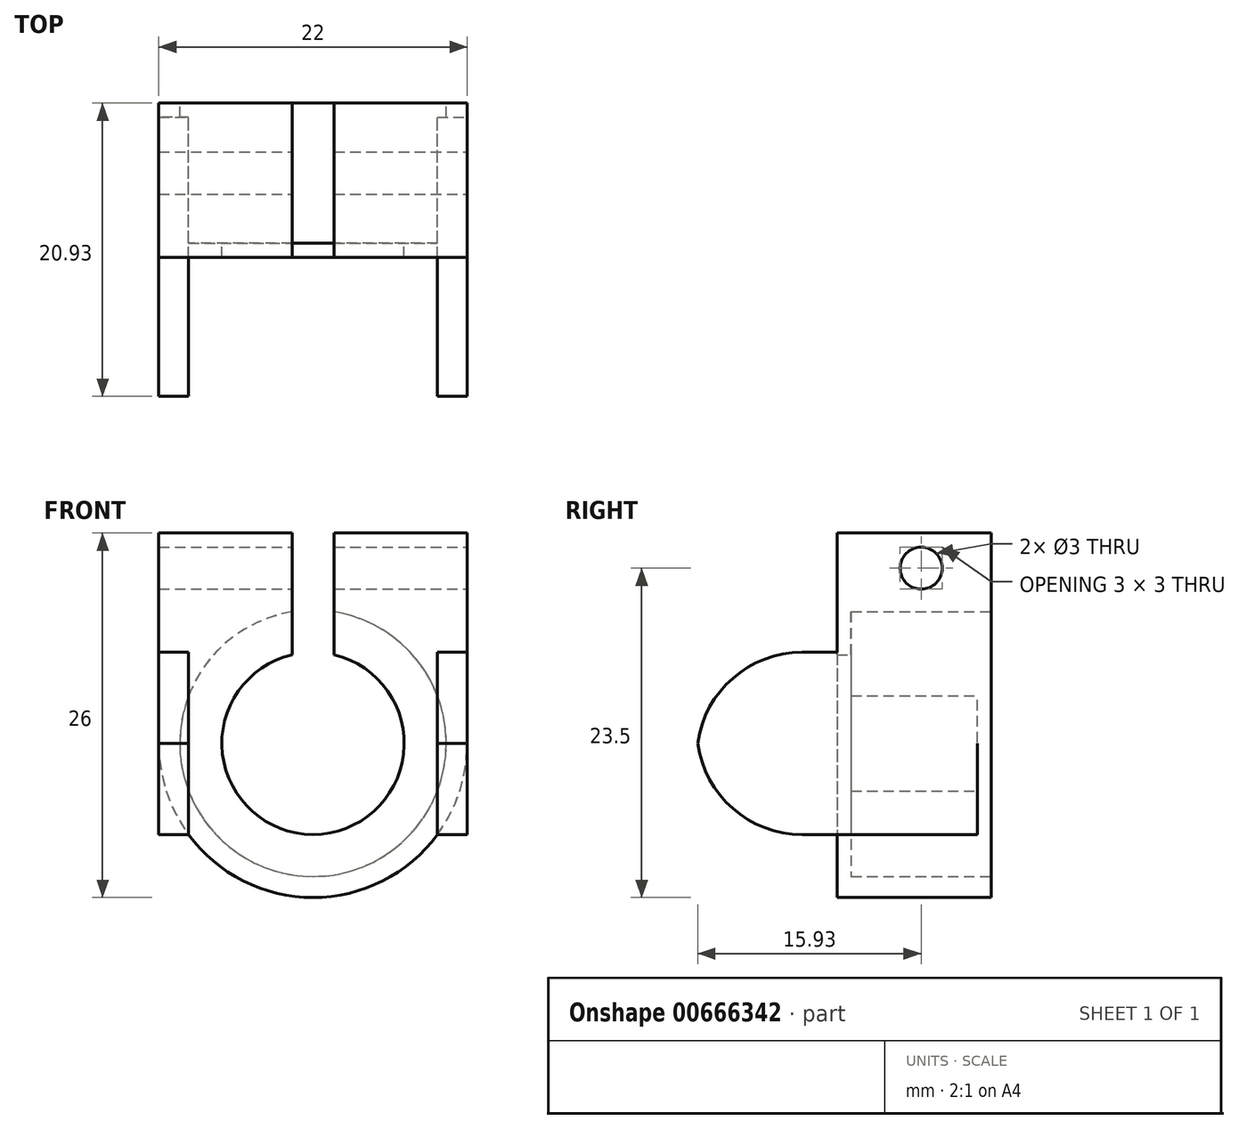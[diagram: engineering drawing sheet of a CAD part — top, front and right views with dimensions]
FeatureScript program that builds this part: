
annotation { "Feature Type Name" : "Feature", "Feature Type Description" : "" }
export const myFeature = defineFeature(function(context is Context, id is Id, definition is map)
    precondition{}
    {
        {
            var Q0;
            Q0=qCreatedBy(makeId("Front.planeOp"),FACE);
            var sketch = newSketch(context, id + "F0", { "sketchPlane" : qUnion([Q0])});
            skArc(sketch, "E0", {"start": v(-1.5, 9.38) * mm, "mid": v(0, -9.5) * mm, "end": v(1.5, 9.38) * mm});
            skArc(sketch, "E1", {"start": v(-11, 0) * mm, "mid": v(0, -11) * mm, "end": v(11, 0) * mm});
            skLineSegment(sketch, "E2", {"start": v(11, 0) * mm, "end": v(11, 15) * mm});
            skLineSegment(sketch, "E3", {"start": v(11, 15) * mm, "end": v(1.5, 15) * mm});
            skLineSegment(sketch, "E4", {"start": v(-11, 15) * mm, "end": v(-11, 0) * mm});
            skLineSegment(sketch, "E5", {"start": v(1.5, 9.38) * mm, "end": v(1.5, 15) * mm});
            skLineSegment(sketch, "E6", {"start": v(-1.5, 9.38) * mm, "end": v(-1.5, 15) * mm});
            skLineSegment(sketch, "E7.trimOffspring", {"start": v(-1.5, 15) * mm, "end": v(-11, 15) * mm});
            skSolve(sketch);
        }
        {
            var Q0;
            Q0=makeQuery(id+"F0.imprint","IMPRINT",FACE,{"disambiguationData":[TD([[makeQuery(id+"F0.imprint","IMPRINT",EDGE,{"derivedFrom":sQuery(id+"F0.wireOp",EDGE,"E0")}),-1.0]])]});
            extrude(context, id + "F1", {"entities" : qUnion([Q0]), "depth" : 10 * mm, "offsetDistance" : 25 * mm});
        }
        {
            var Q0;
            Q0=makeQuery(id+"F1.opExtrude","SWEPT_FACE",FACE,{"disambiguationData":[OSD([sQuery(id+"F0.wireOp",EDGE,"E2")])]});
            var sketch = newSketch(context, id + "F2", { "sketchPlane" : qUnion([Q0])});
            skLineSegment(sketch, "E8.0", {"start": v(-10, 9.38) * mm, "end": v(0, 9.38) * mm});
            skPoint(sketch, "E9", {"position": v(-5, 12.5) * mm});
            skSolve(sketch);
        }
        {
            var Q0;
            Q0=sQuery(id+"F2.wireOp",VERTEX,"E9");
            var Q1;
            Q1=makeQuery(id+"F1.opExtrude","SWEPT_BODY",BODY,{"disambiguationData":[OSD([sQuery(id+"F0.wireOp",EDGE,"E0"),sQuery(id+"F0.wireOp",EDGE,"E1"),sQuery(id+"F0.wireOp",EDGE,"E2"),sQuery(id+"F0.wireOp",EDGE,"E3"),sQuery(id+"F0.wireOp",EDGE,"E4"),sQuery(id+"F0.wireOp",EDGE,"E5"),sQuery(id+"F0.wireOp",EDGE,"E6"),sQuery(id+"F0.wireOp",EDGE,"E7.trimOffspring")])]});
            hole(context, id + "F3", {"style" : HoleStyle.SIMPLE, "endStyle" : HoleEndStyle.THROUGH, "holeDiameter" : 3 * mm, "majorDiameter" : 5 * mm, "isTappedThrough" : true, "tappedDepth" : 12 * mm, "tapClearance" : 3, "locations" : qUnion([Q0]), "scope" : qUnion([Q1])});
        }
        {
            var Q0;
            Q0=makeQuery(id+"F1.opExtrude","CAP_FACE",FACE,{"disambiguationData":[OSD([sQuery(id+"F0.wireOp",EDGE,"E0"),sQuery(id+"F0.wireOp",EDGE,"E1"),sQuery(id+"F0.wireOp",EDGE,"E2"),sQuery(id+"F0.wireOp",EDGE,"E3"),sQuery(id+"F0.wireOp",EDGE,"E4"),sQuery(id+"F0.wireOp",EDGE,"E5"),sQuery(id+"F0.wireOp",EDGE,"E6"),sQuery(id+"F0.wireOp",EDGE,"E7.trimOffspring")])],"isStart":false});
            var sketch = newSketch(context, id + "F4", { "sketchPlane" : qUnion([Q0])});
            skLineSegment(sketch, "E10.0", {"start": v(-11, 15) * mm, "end": v(-11, 0) * mm});
            skLineSegment(sketch, "E11.0", {"start": v(-1.5, 15) * mm, "end": v(-11, 15) * mm});
            skArc(sketch, "E12.0", {"start": v(-11, 0) * mm, "mid": v(0, -11) * mm, "end": v(11, 0) * mm});
            skLineSegment(sketch, "E13.0", {"start": v(11, 0) * mm, "end": v(11, 15) * mm});
            skLineSegment(sketch, "E14.0", {"start": v(11, 15) * mm, "end": v(1.5, 15) * mm});
            skLineSegment(sketch, "E15.0", {"start": v(1.5, 6.32) * mm, "end": v(1.5, 15) * mm});
            skLineSegment(sketch, "E16.0", {"start": v(-1.5, 6.32) * mm, "end": v(-1.5, 15) * mm});
            skArc(sketch, "E17.0", {"start": v(-1.5, 6.32) * mm, "mid": v(0, -6.5) * mm, "end": v(1.5, 6.32) * mm});
            skPoint(sketch, "E18.orphan", {"position": v(-1.5, 9.38) * mm});
            skPoint(sketch, "E19.orphan", {"position": v(1.5, 9.38) * mm});
            skSolve(sketch);
        }
        {
            var Q0;
            Q0 = qSketchRegion(id + "F4", true);
            extrude(context, id + "F5", {"entities" : qUnion([Q0]), "operationType" : NewBodyOperationType.ADD, "depth" : 1 * mm, "offsetDistance" : 25 * mm});
        }
        {
            var Q0;
            Q0=makeQuery(id+"F5.opExtrude","CAP_FACE",FACE,{"disambiguationData":[OSD([sQuery(id+"F4.wireOp",EDGE,"E10.0"),sQuery(id+"F4.wireOp",EDGE,"E11.0"),sQuery(id+"F4.wireOp",EDGE,"E12.0"),sQuery(id+"F4.wireOp",EDGE,"E13.0"),sQuery(id+"F4.wireOp",EDGE,"E14.0"),sQuery(id+"F4.wireOp",EDGE,"E15.0"),sQuery(id+"F4.wireOp",EDGE,"E16.0"),sQuery(id+"F4.wireOp",EDGE,"E17.0")])],"isStart":false});
            var sketch = newSketch(context, id + "F6", { "sketchPlane" : qUnion([Q0])});
            skLineSegment(sketch, "E20.bottom", {"start": v(-8.87, -6.5) * mm, "end": v(-11, -6.5) * mm});
            skLineSegment(sketch, "E20.top", {"start": v(-8.87, 6.5) * mm, "end": v(-11, 6.5) * mm});
            skLineSegment(sketch, "E20.left", {"start": v(-8.87, -6.5) * mm, "end": v(-8.87, 6.5) * mm});
            skPoint(sketch, "E20.middle", {"position": v(-11, 0) * mm});
            skPoint(sketch, "E20.cornerSnap0", {"position": v(0, -6.5) * mm});
            skLineSegment(sketch, "E21", {"start": v(-11, 6.5) * mm, "end": v(-11, -6.5) * mm});
            skPoint(sketch, "E20.right.end.orphan", {"position": v(-13.13, 6.5) * mm});
            skPoint(sketch, "E22.orphan", {"position": v(-13.13, -6.5) * mm});
            skLineSegment(sketch, "E23.MirrorCS", {"start": v(8.87, -6.5) * mm, "end": v(11, -6.5) * mm});
            skPoint(sketch, "E24.MirrorP", {"position": v(11, 0) * mm});
            skLineSegment(sketch, "E25.MirrorCS", {"start": v(11, 6.5) * mm, "end": v(11, -6.5) * mm});
            skLineSegment(sketch, "E26.MirrorCS", {"start": v(8.87, -6.5) * mm, "end": v(8.87, 6.5) * mm});
            skLineSegment(sketch, "E27.MirrorCS", {"start": v(8.87, 6.5) * mm, "end": v(11, 6.5) * mm});
            skSolve(sketch);
        }
        {
            var Q0;
            Q0 = qSketchRegion(id + "F6", true);
            extrude(context, id + "F7", {"entities" : qUnion([Q0]), "operationType" : NewBodyOperationType.ADD, "endBound" : BoundingType.SYMMETRIC, "depth" : 20 * mm, "offsetDistance" : 25 * mm});
        }
        {
            var Q0;
            Q0=makeQuery(id+"F7.opExtrude","CAP_EDGE",EDGE,{"disambiguationData":[OSD([sQuery(id+"F6.wireOp",EDGE,"E20.bottom")])],"isStart":false});
            var Q1;
            Q1=makeQuery(id+"F7.opExtrude","CAP_EDGE",EDGE,{"disambiguationData":[OSD([sQuery(id+"F6.wireOp",EDGE,"E20.top")])],"isStart":false});
            var Q2;
            Q2=makeQuery(id+"F7.opExtrude","CAP_EDGE",EDGE,{"disambiguationData":[OSD([sQuery(id+"F6.wireOp",EDGE,"E27.MirrorCS")])],"isStart":false});
            var Q3;
            Q3=makeQuery(id+"F7.opExtrude","CAP_EDGE",EDGE,{"disambiguationData":[OSD([sQuery(id+"F6.wireOp",EDGE,"E23.MirrorCS")])],"isStart":false});
            fillet(context, id + "F8", {"entities" : qUnion([Q0, Q1, Q2, Q3]), "radius" : 7.5 * mm, "tangentPropagation" : true, "allowEdgeOverflow" : false});
        }
    });
